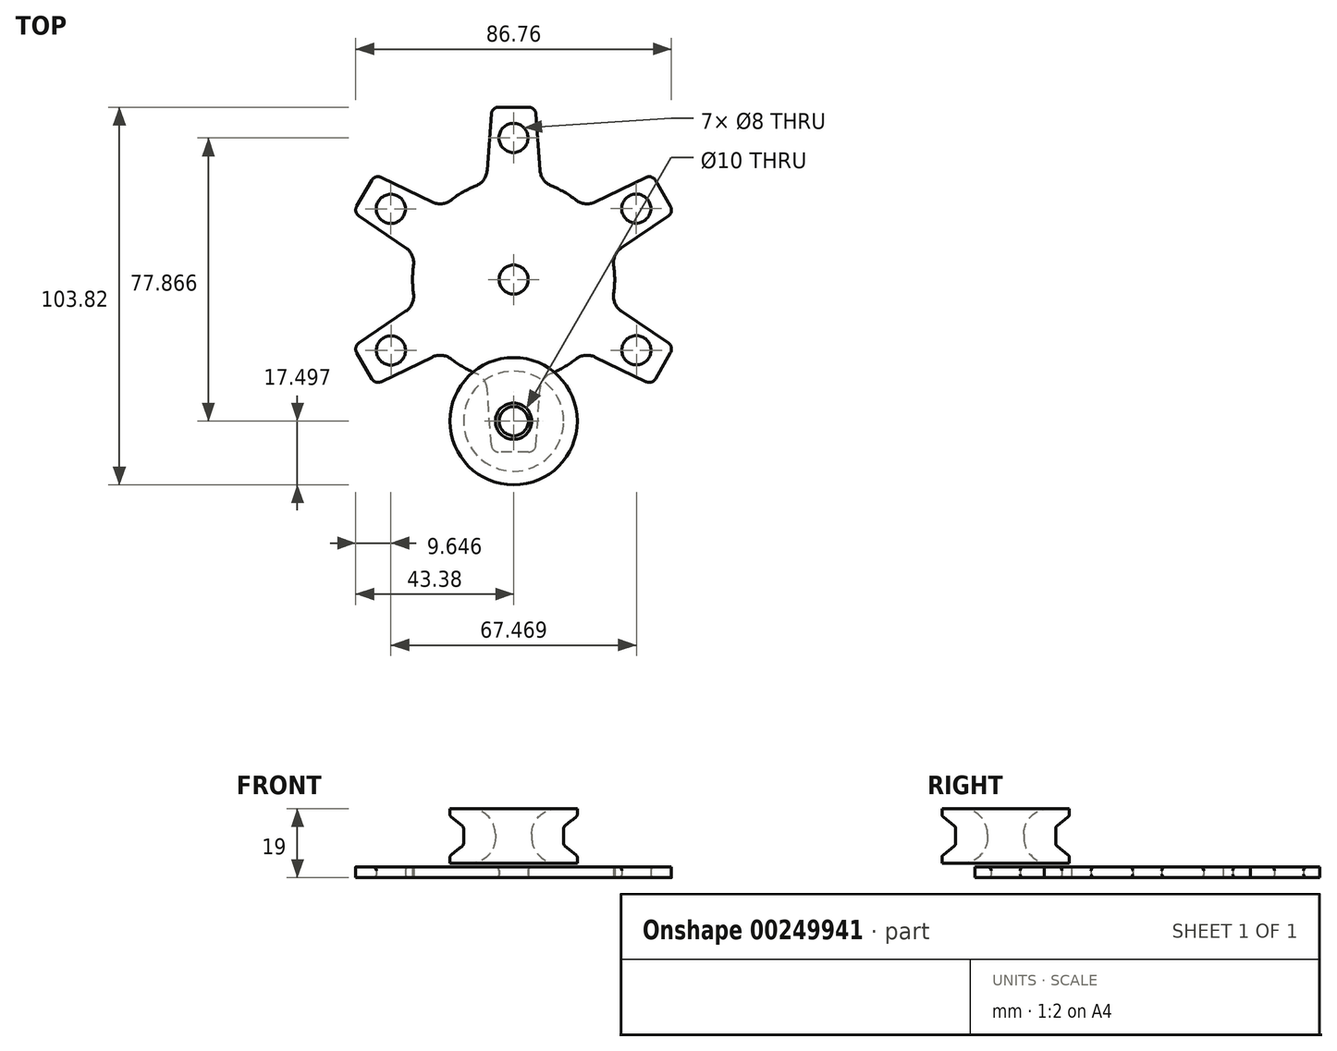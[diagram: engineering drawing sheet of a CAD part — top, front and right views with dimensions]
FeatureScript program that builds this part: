
annotation { "Feature Type Name" : "Feature", "Feature Type Description" : "" }
export const myFeature = defineFeature(function(context is Context, id is Id, definition is map)
    precondition{}
    {
        {
            var Q0;
            Q0=qCreatedBy(makeId("Top.planeOp"),FACE);
            var sketch = newSketch(context, id + "F0", { "sketchPlane" : qUnion([Q0])});
            skCircle(sketch, "E0", {"center": v(0, 0) * mm, "radius": 47.77 * mm, "construction": true});
            skCircle(sketch, "E1", {"center": v(0, 0) * mm, "radius": 27.77 * mm});
            skLineSegment(sketch, "E2", {"start": v(-6, 47.4) * mm, "end": v(-7.5, 26.74) * mm});
            skLineSegment(sketch, "E3", {"start": v(6, 47.4) * mm, "end": v(7.5, 26.74) * mm});
            skLineSegment(sketch, "E4", {"start": v(-7.5, 26.74) * mm, "end": v(7.5, 26.74) * mm, "construction": true});
            skLineSegment(sketch, "E5", {"start": v(-6, 47.4) * mm, "end": v(6, 47.4) * mm});
            skLineSegment(sketch, "E6.1.0", {"start": v(-44.04, 18.5) * mm, "end": v(-38.04, 28.9) * mm});
            skLineSegment(sketch, "E6.1.1", {"start": v(-44.04, 18.5) * mm, "end": v(-26.9, 6.87) * mm});
            skLineSegment(sketch, "E6.1.2", {"start": v(-38.04, 28.9) * mm, "end": v(-19.4, 19.86) * mm});
            skLineSegment(sketch, "E6.2.0", {"start": v(-38.04, -28.9) * mm, "end": v(-44.04, -18.5) * mm});
            skLineSegment(sketch, "E6.2.1", {"start": v(-38.04, -28.9) * mm, "end": v(-19.4, -19.86) * mm});
            skLineSegment(sketch, "E6.2.2", {"start": v(-44.04, -18.5) * mm, "end": v(-26.9, -6.87) * mm});
            skLineSegment(sketch, "E6.3.0", {"start": v(6, -47.4) * mm, "end": v(-6, -47.4) * mm});
            skLineSegment(sketch, "E6.3.1", {"start": v(6, -47.4) * mm, "end": v(7.5, -26.74) * mm});
            skLineSegment(sketch, "E6.3.2", {"start": v(-6, -47.4) * mm, "end": v(-7.5, -26.74) * mm});
            skLineSegment(sketch, "E6.4.0", {"start": v(44.04, -18.5) * mm, "end": v(38.04, -28.9) * mm});
            skLineSegment(sketch, "E6.4.1", {"start": v(44.04, -18.5) * mm, "end": v(26.9, -6.87) * mm});
            skLineSegment(sketch, "E6.4.2", {"start": v(38.04, -28.9) * mm, "end": v(19.4, -19.86) * mm});
            skCircle(sketch, "E7", {"center": v(-33.73, 19.44) * mm, "radius": 4 * mm});
            skCircle(sketch, "E8.1.0", {"center": v(-33.7, -19.5) * mm, "radius": 4 * mm});
            skCircle(sketch, "E8.2.0", {"center": v(0.03, -38.93) * mm, "radius": 4 * mm});
            skCircle(sketch, "E8.3.0", {"center": v(33.73, -19.44) * mm, "radius": 4 * mm});
            skCircle(sketch, "E8.4.0", {"center": v(33.7, 19.5) * mm, "radius": 4 * mm});
            skCircle(sketch, "E9", {"center": v(0, 0) * mm, "radius": 4 * mm});
            skCircle(sketch, "E10", {"center": v(-143.31, 0) * mm, "radius": 3.5 * mm});
            skCircle(sketch, "E11", {"center": v(-143.31, 0) * mm, "radius": 5 * mm});
            skLineSegment(sketch, "E12", {"start": v(-143.31, 0) * mm, "end": v(-143.31, -5) * mm});
            skLineSegment(sketch, "E13", {"start": v(-143.31, -5) * mm, "end": v(-143.31, 5) * mm});
            skLineSegment(sketch, "E14", {"start": v(-30.84, 25.4) * mm, "end": v(-36.63, 13.47) * mm, "construction": true});
            skLineSegment(sketch, "E15.1.5.0", {"start": v(38.04, 28.9) * mm, "end": v(44.04, 18.5) * mm});
            skLineSegment(sketch, "E15.3.5.0", {"start": v(38.04, 28.9) * mm, "end": v(19.4, 19.86) * mm});
            skLineSegment(sketch, "E15.6.5.0", {"start": v(44.04, 18.5) * mm, "end": v(26.9, 6.87) * mm});
            skCircle(sketch, "E16.1.5.0", {"center": v(-0.03, 38.93) * mm, "radius": 4 * mm});
            skSolve(sketch);
        }
        {
            var Q0;
            {var subQ0=sQuery(id+"F0.wireOp",EDGE,"E1");var subQ6=makeQuery(id+"F0.imprint","INTERSECT",VERTEX,{"derivedFrom":[subQ0,sQuery(id+"F0.wireOp",EDGE,"E3")]});Q0=makeQuery(id+"F0.imprint","IMPRINT",FACE,{"disambiguationData":[TD([[makeQuery(id+"F0.imprint","IMPRINT",EDGE,{"disambiguationData":[TD([[subQ6,1.0]])],"derivedFrom":subQ0}),1.0]])]});}
            var Q1;
            Q1=makeQuery(id+"F0.imprint","IMPRINT",FACE,{"disambiguationData":[TD([[makeQuery(id+"F0.imprint","IMPRINT",EDGE,{"derivedFrom":sQuery(id+"F0.wireOp",EDGE,"E6.1.0")}),-1.0]])]});
            var Q2;
            Q2=makeQuery(id+"F0.imprint","IMPRINT",FACE,{"disambiguationData":[TD([[makeQuery(id+"F0.imprint","IMPRINT",EDGE,{"derivedFrom":sQuery(id+"F0.wireOp",EDGE,"E6.2.0")}),-1.0]])]});
            var Q3;
            Q3=makeQuery(id+"F0.imprint","IMPRINT",FACE,{"disambiguationData":[TD([[makeQuery(id+"F0.imprint","IMPRINT",EDGE,{"derivedFrom":sQuery(id+"F0.wireOp",EDGE,"E6.3.0")}),-1.0]])]});
            var Q4;
            Q4=makeQuery(id+"F0.imprint","IMPRINT",FACE,{"disambiguationData":[TD([[makeQuery(id+"F0.imprint","IMPRINT",EDGE,{"derivedFrom":sQuery(id+"F0.wireOp",EDGE,"E6.4.0")}),-1.0]])]});
            var Q5;
            {var subQ0=sQuery(id+"F0.wireOp",EDGE,"E2");Q5=makeQuery(id+"F0.imprint","IMPRINT",FACE,{"disambiguationData":[TD([[makeQuery(id+"F0.imprint","IMPRINT",EDGE,{"derivedFrom":subQ0}),1.0]])]});}
            var Q6;
            Q6=makeQuery(id+"F0.imprint","IMPRINT",FACE,{"disambiguationData":[TD([[makeQuery(id+"F0.imprint","IMPRINT",EDGE,{"derivedFrom":sQuery(id+"F0.wireOp",EDGE,"E8.4.0")}),-1.0]])]});
            extrude(context, id + "F1", {"entities" : qUnion([Q0, Q1, Q2, Q3, Q4, Q5, Q6]), "depth" : 3 * mm});
        }
        {
            var Q0;
            Q0=makeQuery(id+"F1.opExtrude","SWEPT_EDGE",EDGE,{"disambiguationData":[OSD([sQuery(id+"F0.wireOp",EDGE,"E1"),sQuery(id+"F0.wireOp",EDGE,"E6.2.1")])]});
            var Q1;
            Q1=makeQuery(id+"F1.opExtrude","SWEPT_EDGE",EDGE,{"disambiguationData":[OSD([sQuery(id+"F0.wireOp",EDGE,"E1"),sQuery(id+"F0.wireOp",EDGE,"E6.3.2")])]});
            var Q2;
            Q2=makeQuery(id+"F1.opExtrude","SWEPT_EDGE",EDGE,{"disambiguationData":[OSD([sQuery(id+"F0.wireOp",EDGE,"E1"),sQuery(id+"F0.wireOp",EDGE,"E6.4.2")])]});
            var Q3;
            Q3=makeQuery(id+"F1.opExtrude","SWEPT_EDGE",EDGE,{"disambiguationData":[OSD([sQuery(id+"F0.wireOp",EDGE,"E1"),sQuery(id+"F0.wireOp",EDGE,"E6.3.1")])]});
            var Q4;
            Q4=makeQuery(id+"F1.opExtrude","SWEPT_EDGE",EDGE,{"disambiguationData":[OSD([sQuery(id+"F0.wireOp",EDGE,"E1"),sQuery(id+"F0.wireOp",EDGE,"E6.4.1")])]});
            var Q5;
            Q5=makeQuery(id+"F1.opExtrude","SWEPT_EDGE",EDGE,{"disambiguationData":[OSD([sQuery(id+"F0.wireOp",EDGE,"E1"),sQuery(id+"F0.wireOp",EDGE,"E3")])]});
            var Q6;
            Q6=makeQuery(id+"F1.opExtrude","SWEPT_EDGE",EDGE,{"disambiguationData":[OSD([sQuery(id+"F0.wireOp",EDGE,"E1"),sQuery(id+"F0.wireOp",EDGE,"E2")])]});
            var Q7;
            Q7=makeQuery(id+"F1.opExtrude","SWEPT_EDGE",EDGE,{"disambiguationData":[OSD([sQuery(id+"F0.wireOp",EDGE,"E1"),sQuery(id+"F0.wireOp",EDGE,"E6.1.2")])]});
            var Q8;
            Q8=makeQuery(id+"F1.opExtrude","SWEPT_EDGE",EDGE,{"disambiguationData":[OSD([sQuery(id+"F0.wireOp",EDGE,"E1"),sQuery(id+"F0.wireOp",EDGE,"E6.1.1")])]});
            var Q9;
            Q9=makeQuery(id+"F1.opExtrude","SWEPT_EDGE",EDGE,{"disambiguationData":[OSD([sQuery(id+"F0.wireOp",EDGE,"E1"),sQuery(id+"F0.wireOp",EDGE,"E6.2.2")])]});
            var Q10;
            Q10=makeQuery(id+"F1.opExtrude","SWEPT_EDGE",EDGE,{"disambiguationData":[OSD([sQuery(id+"F0.wireOp",EDGE,"E1"),sQuery(id+"F0.wireOp",EDGE,"E15.6.5.0")])]});
            var Q11;
            Q11=makeQuery(id+"F1.opExtrude","SWEPT_EDGE",EDGE,{"disambiguationData":[OSD([sQuery(id+"F0.wireOp",EDGE,"E1"),sQuery(id+"F0.wireOp",EDGE,"E15.3.5.0")])]});
            fillet(context, id + "F2", {"entities" : qUnion([Q0, Q1, Q2, Q3, Q4, Q5, Q6, Q7, Q8, Q9, Q10, Q11]), "radius" : 5 * mm, "tangentPropagation" : true, "allowEdgeOverflow" : false});
        }
        {
            var Q0;
            Q0=makeQuery(id+"F1.opExtrude","SWEPT_EDGE",EDGE,{"disambiguationData":[OSD([sQuery(id+"F0.wireOp",EDGE,"E6.2.0"),sQuery(id+"F0.wireOp",EDGE,"E6.2.2")])]});
            var Q1;
            Q1=makeQuery(id+"F1.opExtrude","SWEPT_EDGE",EDGE,{"disambiguationData":[OSD([sQuery(id+"F0.wireOp",EDGE,"E6.3.0"),sQuery(id+"F0.wireOp",EDGE,"E6.3.2")])]});
            var Q2;
            Q2=makeQuery(id+"F1.opExtrude","SWEPT_EDGE",EDGE,{"disambiguationData":[OSD([sQuery(id+"F0.wireOp",EDGE,"E6.4.0"),sQuery(id+"F0.wireOp",EDGE,"E6.4.2")])]});
            var Q3;
            Q3=makeQuery(id+"F1.opExtrude","SWEPT_EDGE",EDGE,{"disambiguationData":[OSD([sQuery(id+"F0.wireOp",EDGE,"E6.1.0"),sQuery(id+"F0.wireOp",EDGE,"E6.1.2")])]});
            var Q4;
            Q4=makeQuery(id+"F1.opExtrude","SWEPT_EDGE",EDGE,{"disambiguationData":[OSD([sQuery(id+"F0.wireOp",EDGE,"E3"),sQuery(id+"F0.wireOp",EDGE,"E5")])]});
            var Q5;
            Q5=makeQuery(id+"F1.opExtrude","SWEPT_EDGE",EDGE,{"disambiguationData":[OSD([sQuery(id+"F0.wireOp",EDGE,"E2"),sQuery(id+"F0.wireOp",EDGE,"E5")])]});
            var Q6;
            Q6=makeQuery(id+"F1.opExtrude","SWEPT_EDGE",EDGE,{"disambiguationData":[OSD([sQuery(id+"F0.wireOp",EDGE,"E6.1.0"),sQuery(id+"F0.wireOp",EDGE,"E6.1.1")])]});
            var Q7;
            Q7=makeQuery(id+"F1.opExtrude","SWEPT_EDGE",EDGE,{"disambiguationData":[OSD([sQuery(id+"F0.wireOp",EDGE,"E6.4.0"),sQuery(id+"F0.wireOp",EDGE,"E6.4.1")])]});
            var Q8;
            Q8=makeQuery(id+"F1.opExtrude","SWEPT_EDGE",EDGE,{"disambiguationData":[OSD([sQuery(id+"F0.wireOp",EDGE,"E6.3.0"),sQuery(id+"F0.wireOp",EDGE,"E6.3.1")])]});
            var Q9;
            Q9=makeQuery(id+"F1.opExtrude","SWEPT_EDGE",EDGE,{"disambiguationData":[OSD([sQuery(id+"F0.wireOp",EDGE,"E6.2.0"),sQuery(id+"F0.wireOp",EDGE,"E6.2.1")])]});
            var Q10;
            Q10=makeQuery(id+"F1.opExtrude","SWEPT_EDGE",EDGE,{"disambiguationData":[OSD([sQuery(id+"F0.wireOp",EDGE,"E15.1.5.0"),sQuery(id+"F0.wireOp",EDGE,"E15.3.5.0")])]});
            var Q11;
            Q11=makeQuery(id+"F1.opExtrude","SWEPT_EDGE",EDGE,{"disambiguationData":[OSD([sQuery(id+"F0.wireOp",EDGE,"E15.1.5.0"),sQuery(id+"F0.wireOp",EDGE,"E15.6.5.0")])]});
            fillet(context, id + "F3", {"entities" : qUnion([Q0, Q1, Q2, Q3, Q4, Q5, Q6, Q7, Q8, Q9, Q10, Q11]), "radius" : 2 * mm, "tangentPropagation" : true, "allowEdgeOverflow" : false});
        }
        {
            var Q0;
            Q0=makeQuery(id+"F1.opExtrude","CAP_EDGE",EDGE,{"disambiguationData":[OSD([sQuery(id+"F0.wireOp",EDGE,"E9")])],"isStart":false});
            var Q1;
            Q1=makeQuery(id+"F1.opExtrude","CAP_EDGE",EDGE,{"disambiguationData":[OSD([sQuery(id+"F0.wireOp",EDGE,"E8.1.0")])],"isStart":false});
            var Q2;
            Q2=makeQuery(id+"F1.opExtrude","CAP_EDGE",EDGE,{"disambiguationData":[OSD([sQuery(id+"F0.wireOp",EDGE,"E7")])],"isStart":false});
            var Q3;
            Q3=makeQuery(id+"F1.opExtrude","CAP_EDGE",EDGE,{"disambiguationData":[OSD([sQuery(id+"F0.wireOp",EDGE,"E8.2.0")])],"isStart":false});
            var Q4;
            Q4=makeQuery(id+"F1.opExtrude","CAP_EDGE",EDGE,{"disambiguationData":[OSD([sQuery(id+"F0.wireOp",EDGE,"E8.3.0")])],"isStart":false});
            var Q5;
            Q5=makeQuery(id+"F1.opExtrude","CAP_EDGE",EDGE,{"disambiguationData":[OSD([sQuery(id+"F0.wireOp",EDGE,"E8.4.0")])],"isStart":false});
            var Q6;
            Q6=makeQuery(id+"F1.opExtrude","CAP_EDGE",EDGE,{"disambiguationData":[OSD([sQuery(id+"F0.wireOp",EDGE,"E7")])],"isStart":true});
            var Q7;
            Q7=makeQuery(id+"F1.opExtrude","CAP_EDGE",EDGE,{"disambiguationData":[OSD([sQuery(id+"F0.wireOp",EDGE,"E8.4.0")])],"isStart":true});
            var Q8;
            Q8=makeQuery(id+"F1.opExtrude","CAP_EDGE",EDGE,{"disambiguationData":[OSD([sQuery(id+"F0.wireOp",EDGE,"E9")])],"isStart":true});
            var Q9;
            Q9=makeQuery(id+"F1.opExtrude","CAP_EDGE",EDGE,{"disambiguationData":[OSD([sQuery(id+"F0.wireOp",EDGE,"E8.3.0")])],"isStart":true});
            var Q10;
            Q10=makeQuery(id+"F1.opExtrude","CAP_EDGE",EDGE,{"disambiguationData":[OSD([sQuery(id+"F0.wireOp",EDGE,"E8.2.0")])],"isStart":true});
            var Q11;
            Q11=makeQuery(id+"F1.opExtrude","CAP_EDGE",EDGE,{"disambiguationData":[OSD([sQuery(id+"F0.wireOp",EDGE,"E8.1.0")])],"isStart":true});
            var Q12;
            Q12=makeQuery(id+"F1.opExtrude","CAP_EDGE",EDGE,{"disambiguationData":[OSD([sQuery(id+"F0.wireOp",EDGE,"E16.1.5.0")])],"isStart":false});
            var Q13;
            Q13=makeQuery(id+"F1.opExtrude","CAP_EDGE",EDGE,{"disambiguationData":[OSD([sQuery(id+"F0.wireOp",EDGE,"E16.1.5.0")])],"isStart":true});
            fillet(context, id + "F4", {"entities" : qUnion([Q0, Q1, Q2, Q3, Q4, Q5, Q6, Q7, Q8, Q9, Q10, Q11, Q12, Q13]), "radius" : 1 * mm, "tangentPropagation" : true, "allowEdgeOverflow" : false});
        }
        {
            var Q0;
            Q0=sQuery(id+"F0.wireOp",EDGE,"E11");
            var Q1;
            Q1=sQuery(id+"F0.wireOp",VERTEX,"E13.start");
            cPlane(context, id + "F5", {"entities" : qUnion([Q0, Q1]), "cplaneType" : CPlaneType.CURVE_POINT, "offset" : 25 * mm, "width" : 150 * mm, "height" : 150 * mm});
        }
        {
            var Q0;
            Q0=qCreatedBy(makeId("Right.planeOp"),FACE);
            var sketch = newSketch(context, id + "F6", { "sketchPlane" : qUnion([Q0])});
            skLineSegment(sketch, "E17", {"start": v(-38.93, -8.68) * mm, "end": v(-38.93, 16.71) * mm, "construction": true});
            skLineSegment(sketch, "E18", {"start": v(-38.93, 2) * mm, "end": v(-29.55, 2) * mm, "construction": true});
            skLineSegment(sketch, "E19", {"start": v(-33.93, 4) * mm, "end": v(-33.93, 19) * mm});
            skLineSegment(sketch, "E20", {"start": v(-33.93, 19) * mm, "end": v(-21.43, 19) * mm});
            skLineSegment(sketch, "E21", {"start": v(-21.43, 19) * mm, "end": v(-21.43, 17) * mm});
            skLineSegment(sketch, "E22", {"start": v(-21.43, 17) * mm, "end": v(-25.18, 14) * mm});
            skLineSegment(sketch, "E23", {"start": v(-25.18, 14) * mm, "end": v(-25.18, 9) * mm});
            skLineSegment(sketch, "E24", {"start": v(-25.18, 9) * mm, "end": v(-21.43, 6) * mm});
            skLineSegment(sketch, "E25", {"start": v(-21.43, 6) * mm, "end": v(-21.43, 4) * mm});
            skLineSegment(sketch, "E26", {"start": v(-21.43, 4) * mm, "end": v(-33.93, 4) * mm});
            skPoint(sketch, "E27", {"position": v(-33.93, 11.5) * mm});
            skPoint(sketch, "E28", {"position": v(-25.18, 11.5) * mm});
            skLineSegment(sketch, "E29", {"start": v(-33.93, 11.5) * mm, "end": v(-25.18, 11.5) * mm, "construction": true});
            skSolve(sketch);
        }
        {
            var Q0;
            Q0=makeQuery(id+"F6.imprint","IMPRINT",FACE,{"disambiguationData":[TD([[makeQuery(id+"F6.imprint","IMPRINT",EDGE,{"derivedFrom":sQuery(id+"F6.wireOp",EDGE,"E19")}),-1.0]])]});
            var Q1;
            Q1=sQuery(id+"F6.wireOp",EDGE,"E20");
            var Q2;
            Q2=sQuery(id+"F6.wireOp",EDGE,"E19");
            var Q3;
            Q3=sQuery(id+"F6.wireOp",EDGE,"E26");
            var Q4;
            Q4=sQuery(id+"F6.wireOp",EDGE,"E17");
            revolve(context, id + "F7", {"entities" : qUnion([Q0]), "surfaceEntities" : qUnion([Q1, Q2, Q3]), "axis" : qUnion([Q4]), "revolveType" : RevolveType.FULL});
        }
        {
            var Q0;
            Q0=makeQuery(id+"F7.opRevolve","SWEPT_EDGE",EDGE,{"disambiguationData":[OSD([sQuery(id+"F6.wireOp",EDGE,"E23"),sQuery(id+"F6.wireOp",EDGE,"E24")])]});
            var Q1;
            Q1=makeQuery(id+"F7.opRevolve","SWEPT_EDGE",EDGE,{"disambiguationData":[OSD([sQuery(id+"F6.wireOp",EDGE,"E22"),sQuery(id+"F6.wireOp",EDGE,"E23")])]});
            var Q2;
            Q2=makeQuery(id+"F7.opRevolve","SWEPT_EDGE",EDGE,{"disambiguationData":[OSD([sQuery(id+"F6.wireOp",EDGE,"E21"),sQuery(id+"F6.wireOp",EDGE,"E22")])]});
            var Q3;
            Q3=makeQuery(id+"F7.opRevolve","SWEPT_EDGE",EDGE,{"disambiguationData":[OSD([sQuery(id+"F6.wireOp",EDGE,"E24"),sQuery(id+"F6.wireOp",EDGE,"E25")])]});
            fillet(context, id + "F8", {"entities" : qUnion([Q0, Q1, Q2, Q3]), "radius" : 1 * mm, "tangentPropagation" : true, "allowEdgeOverflow" : false});
        }
        {
            var Q0;
            Q0=makeQuery(id+"F7.opRevolve","SWEPT_EDGE",EDGE,{"disambiguationData":[OSD([sQuery(id+"F6.wireOp",EDGE,"E19"),sQuery(id+"F6.wireOp",EDGE,"E20")])]});
            var Q1;
            Q1=makeQuery(id+"F7.opRevolve","SWEPT_EDGE",EDGE,{"disambiguationData":[OSD([sQuery(id+"F6.wireOp",EDGE,"E19"),sQuery(id+"F6.wireOp",EDGE,"E26")])]});
            fillet(context, id + "F9", {"entities" : qUnion([Q0, Q1]), "radius" : 7 * mm, "tangentPropagation" : true, "allowEdgeOverflow" : false});
        }
    });
